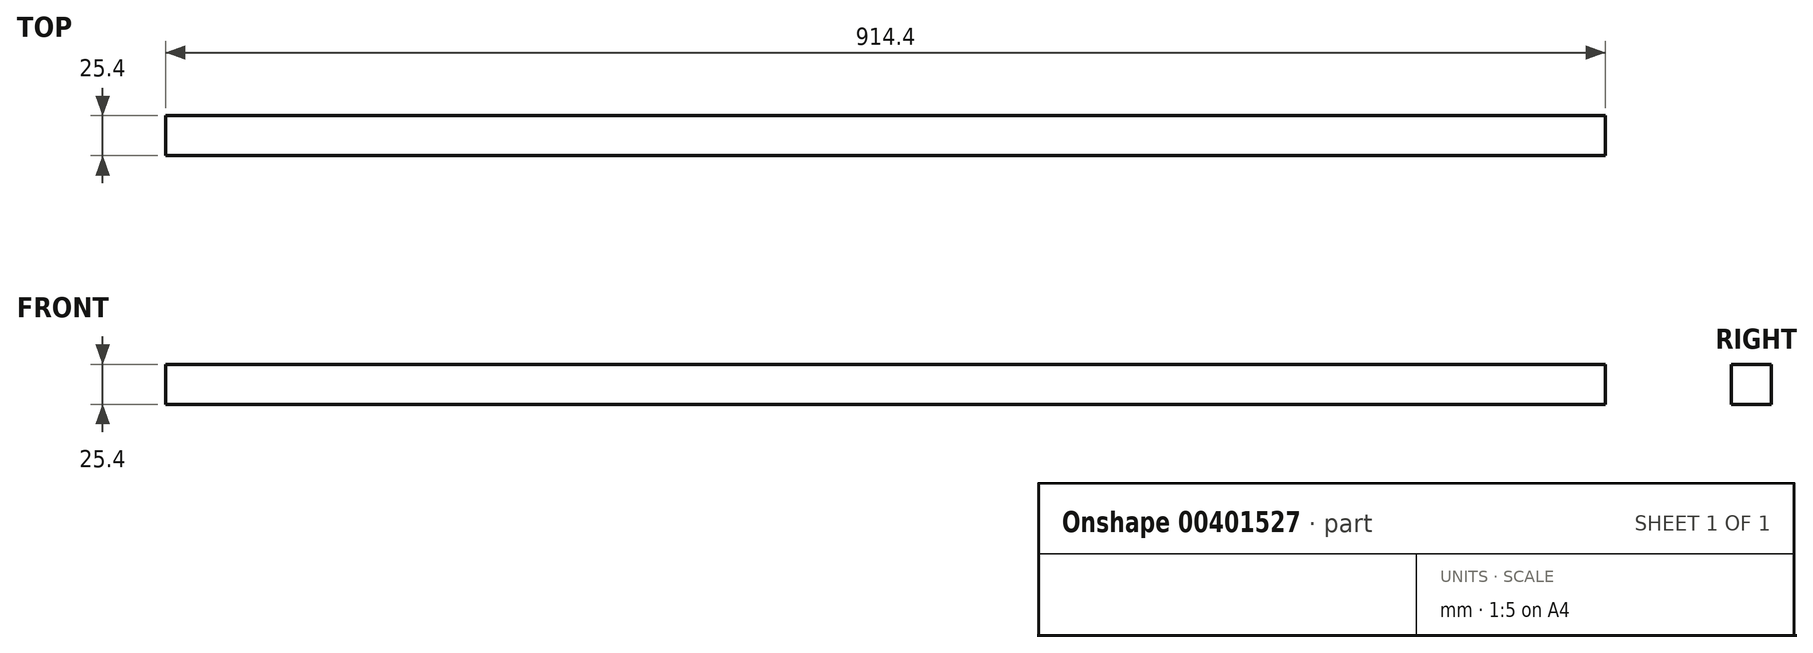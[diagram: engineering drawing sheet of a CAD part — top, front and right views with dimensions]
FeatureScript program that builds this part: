
annotation { "Feature Type Name" : "Feature", "Feature Type Description" : "" }
export const myFeature = defineFeature(function(context is Context, id is Id, definition is map)
    precondition{}
    {
        {
            var Q0;
            Q0=qCreatedBy(makeId("Front.planeOp"),FACE);
            var sketch = newSketch(context, id + "F0", { "sketchPlane" : qUnion([Q0])});
            skLineSegment(sketch, "E0.bottom", {"start": v(-457.2, -12.7) * mm, "end": v(457.2, -12.7) * mm});
            skLineSegment(sketch, "E0.top", {"start": v(-457.2, 12.7) * mm, "end": v(457.2, 12.7) * mm});
            skLineSegment(sketch, "E0.left", {"start": v(-457.2, -12.7) * mm, "end": v(-457.2, 12.7) * mm});
            skLineSegment(sketch, "E0.right", {"start": v(457.2, -12.7) * mm, "end": v(457.2, 12.7) * mm});
            skPoint(sketch, "E0.middle", {"position": v(0, 0) * mm});
            skSolve(sketch);
        }
        {
            var Q0;
            Q0=makeQuery(id+"F0.imprint","IMPRINT",FACE,{"disambiguationData":[TD([[makeQuery(id+"F0.imprint","IMPRINT",EDGE,{"derivedFrom":sQuery(id+"F0.wireOp",EDGE,"E0.bottom")}),1.0]])]});
            extrude(context, id + "F1", {"entities" : qUnion([Q0]), "depth" : 25.4 * mm});
        }
    });
